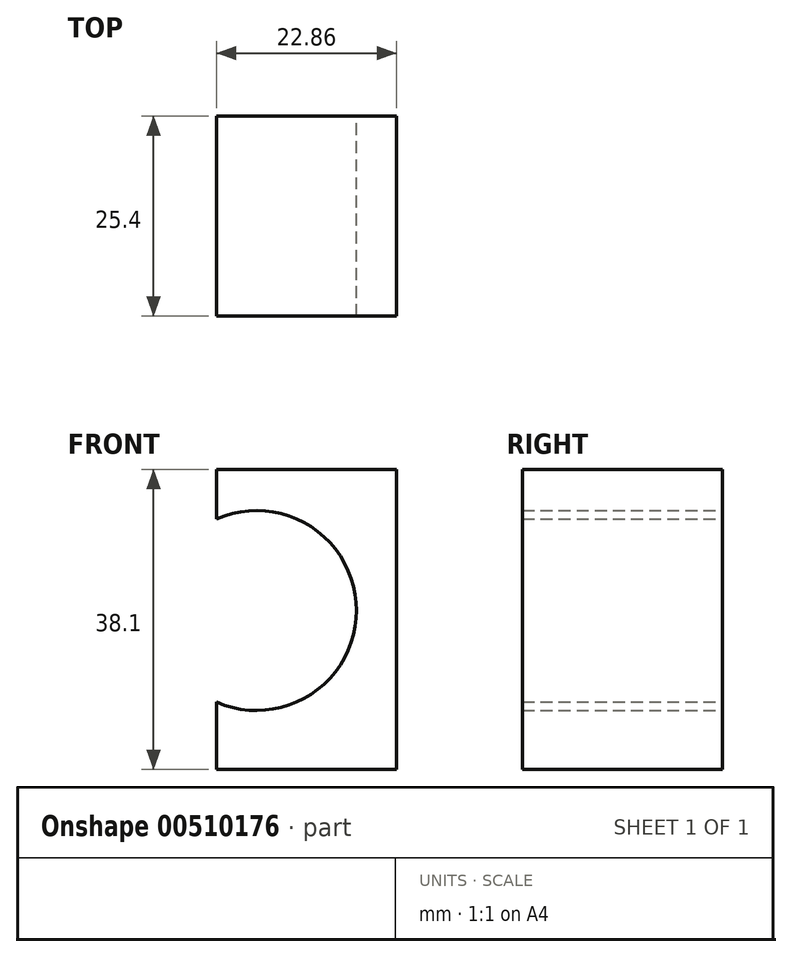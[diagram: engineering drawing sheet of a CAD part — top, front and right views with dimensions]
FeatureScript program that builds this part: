
annotation { "Feature Type Name" : "Feature", "Feature Type Description" : "" }
export const myFeature = defineFeature(function(context is Context, id is Id, definition is map)
    precondition{}
    {
        {
            var Q0;
            Q0=qCreatedBy(makeId("Front.planeOp"),FACE);
            var sketch = newSketch(context, id + "F0", { "sketchPlane" : qUnion([Q0])});
            skLineSegment(sketch, "E0.bottom", {"start": v(-46.27, 17.91) * mm, "end": v(-23.41, 17.91) * mm});
            skLineSegment(sketch, "E0.top", {"start": v(-46.27, -20.19) * mm, "end": v(-23.41, -20.19) * mm});
            skLineSegment(sketch, "E0.left", {"start": v(-46.27, 17.91) * mm, "end": v(-46.27, -20.19) * mm});
            skLineSegment(sketch, "E0.right", {"start": v(-23.41, 17.91) * mm, "end": v(-23.41, -20.19) * mm});
            skSolve(sketch);
        }
        {
            var Q0;
            Q0=makeQuery(id+"F0.imprint","IMPRINT",FACE,{"disambiguationData":[TD([[makeQuery(id+"F0.imprint","IMPRINT",EDGE,{"derivedFrom":sQuery(id+"F0.wireOp",EDGE,"E0.bottom")}),-1.0]])]});
            extrude(context, id + "F1", {"entities" : qUnion([Q0]), "depth" : 25.4 * mm});
        }
        {
            var Q0;
            Q0=qCreatedBy(makeId("Front.planeOp"),FACE);
            var sketch = newSketch(context, id + "F2", { "sketchPlane" : qUnion([Q0])});
            skCircle(sketch, "E1", {"center": v(-35.36, 3.8) * mm, "radius": 12.7 * mm});
            skSolve(sketch);
        }
        {
            var Q0;
            Q0 = qSketchRegion(id + "F2", true);
            extrude(context, id + "F3", {"entities" : qUnion([Q0]), "operationType" : NewBodyOperationType.REMOVE, "endBound" : BoundingType.THROUGH_ALL, "oppositeDirection" : true, "depth" : 25.4 * mm});
        }
        {
            var Q0;
            Q0=makeQuery(id+"F1.opExtrude","CAP_FACE",FACE,{"disambiguationData":[OSD([sQuery(id+"F0.wireOp",EDGE,"E0.bottom"),sQuery(id+"F0.wireOp",EDGE,"E0.top"),sQuery(id+"F0.wireOp",EDGE,"E0.left"),sQuery(id+"F0.wireOp",EDGE,"E0.right")])],"isStart":true});
            var sketch = newSketch(context, id + "F4", { "sketchPlane" : qUnion([Q0])});
            skCircle(sketch, "E2", {"center": v(41.2, 0) * mm, "radius": 12.7 * mm});
            skSolve(sketch);
        }
        {
            var Q0;
            {var subQ0=sQuery(id+"F4.wireOp",EDGE,"E2");var subQ1=makeQuery(id+"F1.opExtrude","CAP_EDGE",EDGE,{"disambiguationData":[OSD([sQuery(id+"F0.wireOp",EDGE,"E0.left")])],"isStart":true});var subQ2=makeQuery(id+"F4.imprint","INTERSECT",VERTEX,{"disambiguationData":[OD(0.0)],"derivedFrom":[subQ1,subQ0]});Q0=makeQuery(id+"F4.imprint","IMPRINT",FACE,{"disambiguationData":[TD([[makeQuery(id+"F4.imprint","IMPRINT",EDGE,{"disambiguationData":[TD([[subQ2,1.0]])],"derivedFrom":subQ0}),1.0]])]});}
            var Q1;
            {var subQ0=sQuery(id+"F4.wireOp",EDGE,"E2");var subQ1=makeQuery(id+"F1.opExtrude","CAP_EDGE",EDGE,{"disambiguationData":[OSD([sQuery(id+"F0.wireOp",EDGE,"E0.left")])],"isStart":true});var subQ2=makeQuery(id+"F4.imprint","INTERSECT",VERTEX,{"disambiguationData":[OD(0.0)],"derivedFrom":[subQ1,subQ0]});Q1=makeQuery(id+"F4.imprint","IMPRINT",FACE,{"disambiguationData":[TD([[makeQuery(id+"F4.imprint","IMPRINT",EDGE,{"disambiguationData":[TD([[subQ2,-1.0]])],"derivedFrom":subQ0}),1.0]])]});}
            extrude(context, id + "F5", {"entities" : qUnion([Q0, Q1]), "operationType" : NewBodyOperationType.REMOVE, "endBound" : BoundingType.THROUGH_ALL, "oppositeDirection" : true, "depth" : 25.4 * mm});
        }
    });
